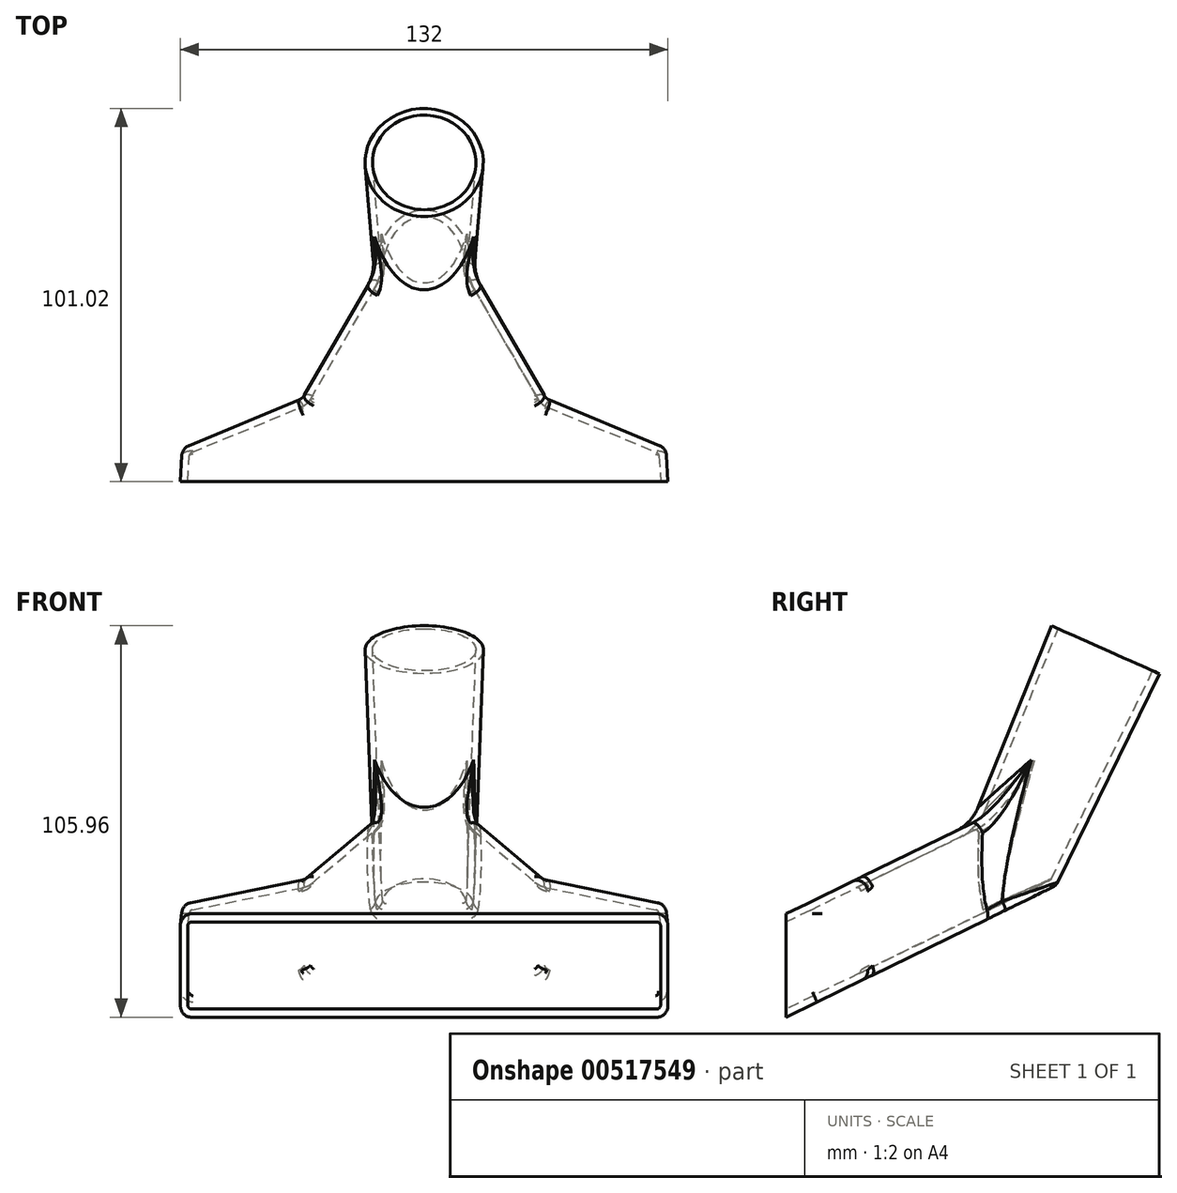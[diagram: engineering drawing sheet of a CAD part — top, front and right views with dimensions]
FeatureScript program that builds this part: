
annotation { "Feature Type Name" : "Feature", "Feature Type Description" : "" }
export const myFeature = defineFeature(function(context is Context, id is Id, definition is map)
    precondition{}
    {
        {
            var Q0;
            Q0=qCreatedBy(makeId("Right.planeOp"),FACE);
            var sketch = newSketch(context, id + "F0", { "sketchPlane" : qUnion([Q0])});
            skLineSegment(sketch, "E0", {"start": v(0, 0) * mm, "end": v(61.84, 30.16) * mm});
            skLineSegment(sketch, "E1", {"start": v(61.84, 30.16) * mm, "end": v(86.44, 85.43) * mm});
            skLineSegment(sketch, "E2", {"start": v(50.13, 0) * mm, "end": v(-17.29, 0) * mm, "construction": true});
            skSolve(sketch);
        }
        {
            var Q0;
            Q0=qCreatedBy(makeId("Top.planeOp"),FACE);
            var sketch = newSketch(context, id + "F1", { "sketchPlane" : qUnion([Q0])});
            skPoint(sketch, "E3", {"position": v(56.62, 0) * mm});
            skSolve(sketch);
        }
        {
            var Q0;
            Q0=sQuery(id+"F1.wireOp",VERTEX,"E3");
            var Q1;
            Q1=sQuery(id+"F0.wireOp",VERTEX,"E1.start");
            var Q2;
            Q2=sQuery(id+"F0.wireOp",VERTEX,"E0.start");
            cPlane(context, id + "F2", {"entities" : qUnion([Q0, Q1, Q2]), "cplaneType" : CPlaneType.THREE_POINT, "offset" : 25 * mm, "width" : 150 * mm, "height" : 150 * mm});
        }
        {
            var Q0;
            Q0=qCreatedBy(id+"F2.planeOp",FACE);
            var sketch = newSketch(context, id + "F3", { "sketchPlane" : qUnion([Q0])});
            skLineSegment(sketch, "E4", {"start": v(66, 0) * mm, "end": v(65.48, -10) * mm});
            skLineSegment(sketch, "E5", {"start": v(10.62, -68) * mm, "end": v(33, -25) * mm});
            skLineSegment(sketch, "E6", {"start": v(0, 33.94) * mm, "end": v(0, -95.34) * mm, "construction": true});
            skLineSegment(sketch, "E7.MirrorCS", {"start": v(-66, 0) * mm, "end": v(-65.48, -10) * mm});
            skLineSegment(sketch, "E8.MirrorCS", {"start": v(-65.48, -10) * mm, "end": v(-33, -25) * mm});
            skLineSegment(sketch, "E9.MirrorCS", {"start": v(-10.62, -68) * mm, "end": v(-33, -25) * mm});
            skLineSegment(sketch, "E10", {"start": v(66, 0) * mm, "end": v(-66, 0) * mm});
            skLineSegment(sketch, "E11", {"start": v(10.62, -68) * mm, "end": v(-10.62, -68) * mm});
            skLineSegment(sketch, "E12", {"start": v(65.48, -10) * mm, "end": v(33, -25) * mm});
            skSolve(sketch);
        }
        {
            var Q0;
            Q0=qCreatedBy(makeId("Front.planeOp"),FACE);
            var sketch = newSketch(context, id + "F4", { "sketchPlane" : qUnion([Q0])});
            skLineSegment(sketch, "E13", {"start": v(0, 0) * mm, "end": v(0, 14) * mm});
            skSolve(sketch);
        }
        {
            var Q0;
            Q0=qCreatedBy(makeId("Front.planeOp"),FACE);
            var sketch = newSketch(context, id + "F5", { "sketchPlane" : qUnion([Q0])});
            skLineSegment(sketch, "E14", {"start": v(0, 0) * mm, "end": v(0, -14) * mm});
            skSolve(sketch);
        }
        {
            var Q0;
            Q0 = qSketchRegion(id + "F3", true);
            var Q1;
            Q1=sQuery(id+"F4.wireOp",EDGE,"E13");
            sweep(context, id + "F6", {"profiles" : qUnion([Q0]), "path" : qUnion([Q1])});
        }
        {
            var Q0;
            Q0 = qSketchRegion(id + "F3", true);
            var Q1;
            Q1=sQuery(id+"F5.wireOp",EDGE,"E14");
            sweep(context, id + "F7", {"operationType" : NewBodyOperationType.ADD, "profiles" : qUnion([Q0]), "path" : qUnion([Q1])});
        }
        {
            var Q0;
            Q0=sQuery(id+"F0.wireOp",EDGE,"E1");
            var Q1;
            Q1=sQuery(id+"F0.wireOp",VERTEX,"E1.end");
            cPlane(context, id + "F8", {"entities" : qUnion([Q0, Q1]), "cplaneType" : CPlaneType.LINE_POINT, "offset" : 25 * mm, "width" : 150 * mm, "height" : 150 * mm});
        }
        {
            var Q0;
            Q0=qCreatedBy(id+"F8.planeOp",FACE);
            var sketch = newSketch(context, id + "F9", { "sketchPlane" : qUnion([Q0])});
            skPoint(sketch, "E15.0", {"position": v(0, 44.22) * mm});
            skCircle(sketch, "E16", {"center": v(0, 44.17) * mm, "radius": 16 * mm});
            skSolve(sketch);
        }
        {
            var Q0;
            Q0 = qSketchRegion(id + "F9", true);
            var Q1;
            Q1=makeQuery(id+"F7.opSweep","CAP_FACE",FACE,{"disambiguationData":[OSD([sQuery(id+"F3.wireOp",EDGE,"E4"),sQuery(id+"F3.wireOp",EDGE,"E5"),sQuery(id+"F3.wireOp",EDGE,"E7.MirrorCS"),sQuery(id+"F3.wireOp",EDGE,"E8.MirrorCS"),sQuery(id+"F3.wireOp",EDGE,"E9.MirrorCS"),sQuery(id+"F3.wireOp",EDGE,"E10"),sQuery(id+"F3.wireOp",EDGE,"E11"),sQuery(id+"F3.wireOp",EDGE,"E12"),sQuery(id+"F5.wireOp",VERTEX,"E14.end")])],"isStart":false});
            var Q2;
            Q2=makeQuery(id+"F7.opSweep","CAP_VERTEX",VERTEX,{"disambiguationData":[OSD([sQuery(id+"F3.wireOp",EDGE,"E5"),sQuery(id+"F3.wireOp",EDGE,"E11"),sQuery(id+"F5.wireOp",EDGE,"E14")])],"isStart":false});
            extrude(context, id + "F10", {"entities" : qUnion([Q0]), "operationType" : NewBodyOperationType.ADD, "endBound" : BoundingType.UP_TO_SURFACE, "oppositeDirection" : true, "depth" : 25 * mm, "endBoundEntityFace" : qUnion([Q1]), "endBoundEntityVertex" : qUnion([Q2]), "offsetDistance" : 25 * mm, "hasDraft" : true, "draftAngle" : 2 * degree, "draftPullDirection" : true});
        }
        {
            var Q0;
            Q0=makeQuery(id+"F10.boolean.opBoolean","INTERSECT",EDGE,{"derivedFrom":[makeQuery(id+"F6.opSweep","CAP_FACE",FACE,{"disambiguationData":[OSD([sQuery(id+"F3.wireOp",EDGE,"E4"),sQuery(id+"F3.wireOp",EDGE,"E5"),sQuery(id+"F3.wireOp",EDGE,"E7.MirrorCS"),sQuery(id+"F3.wireOp",EDGE,"E8.MirrorCS"),sQuery(id+"F3.wireOp",EDGE,"E9.MirrorCS"),sQuery(id+"F3.wireOp",EDGE,"E10"),sQuery(id+"F3.wireOp",EDGE,"E11"),sQuery(id+"F3.wireOp",EDGE,"E12"),sQuery(id+"F4.wireOp",VERTEX,"E13.end")])],"isStart":false}),makeQuery(id+"F10.opExtrude","SWEPT_FACE",FACE,{"disambiguationData":[OSD([sQuery(id+"F9.wireOp",EDGE,"E16")])]})]});
            var Q1;
            {var subQ0=sQuery(id+"F3.wireOp",EDGE,"E5");Q1=makeQuery(id+"F10.boolean.opBoolean","INTERSECT",EDGE,{"derivedFrom":[makeQuery(id+"F7.boolean.opBoolean","MERGE",FACE,{"derivedFrom":[makeQuery(id+"F6.opSweep","SWEPT_FACE",FACE,{"disambiguationData":[OSD([subQ0,sQuery(id+"F4.wireOp",EDGE,"E13")])]}),makeQuery(id+"F7.opSweep","SWEPT_FACE",FACE,{"disambiguationData":[OSD([subQ0,sQuery(id+"F5.wireOp",EDGE,"E14")])]})]}),makeQuery(id+"F10.opExtrude","SWEPT_FACE",FACE,{"disambiguationData":[OSD([sQuery(id+"F9.wireOp",EDGE,"E16")])]})]});}
            var Q2;
            {var subQ0=sQuery(id+"F3.wireOp",EDGE,"E9.MirrorCS");Q2=makeQuery(id+"F10.boolean.opBoolean","INTERSECT",EDGE,{"derivedFrom":[makeQuery(id+"F7.boolean.opBoolean","MERGE",FACE,{"derivedFrom":[makeQuery(id+"F6.opSweep","SWEPT_FACE",FACE,{"disambiguationData":[OSD([subQ0,sQuery(id+"F4.wireOp",EDGE,"E13")])]}),makeQuery(id+"F7.opSweep","SWEPT_FACE",FACE,{"disambiguationData":[OSD([subQ0,sQuery(id+"F5.wireOp",EDGE,"E14")])]})]}),makeQuery(id+"F10.opExtrude","SWEPT_FACE",FACE,{"disambiguationData":[OSD([sQuery(id+"F9.wireOp",EDGE,"E16")])]})]});}
            fillet(context, id + "F11", {"entities" : qUnion([Q0, Q1, Q2]), "radius" : 12 * mm, "tangentPropagation" : true, "allowEdgeOverflow" : false});
        }
        {
            var Q0;
            Q0=makeQuery(id+"F6.opSweep","CAP_EDGE",EDGE,{"disambiguationData":[OSD([sQuery(id+"F3.wireOp",EDGE,"E5"),sQuery(id+"F4.wireOp",VERTEX,"E13.end")])],"isStart":false});
            var Q1;
            Q1=makeQuery(id+"F6.opSweep","CAP_EDGE",EDGE,{"disambiguationData":[OSD([sQuery(id+"F3.wireOp",EDGE,"E12"),sQuery(id+"F4.wireOp",VERTEX,"E13.end")])],"isStart":false});
            var Q2;
            {var subQ0=sQuery(id+"F3.wireOp",EDGE,"E12");var subQ1=sQuery(id+"F3.wireOp",EDGE,"E4");Q2=makeQuery(id+"F7.boolean.opBoolean","MERGE",EDGE,{"derivedFrom":[makeQuery(id+"F6.opSweep","SWEPT_EDGE",EDGE,{"disambiguationData":[OSD([subQ1,subQ0,sQuery(id+"F4.wireOp",EDGE,"E13")])]}),makeQuery(id+"F7.opSweep","SWEPT_EDGE",EDGE,{"disambiguationData":[OSD([subQ1,subQ0,sQuery(id+"F5.wireOp",EDGE,"E14")])]})]});}
            var Q3;
            Q3=makeQuery(id+"F6.opSweep","CAP_EDGE",EDGE,{"disambiguationData":[OSD([sQuery(id+"F3.wireOp",EDGE,"E4"),sQuery(id+"F4.wireOp",VERTEX,"E13.end")])],"isStart":false});
            var Q4;
            Q4=makeQuery(id+"F7.opSweep","CAP_EDGE",EDGE,{"disambiguationData":[OSD([sQuery(id+"F3.wireOp",EDGE,"E4"),sQuery(id+"F5.wireOp",VERTEX,"E14.end")])],"isStart":false});
            var Q5;
            Q5=makeQuery(id+"F7.opSweep","CAP_EDGE",EDGE,{"disambiguationData":[OSD([sQuery(id+"F3.wireOp",EDGE,"E5"),sQuery(id+"F5.wireOp",VERTEX,"E14.end")])],"isStart":false});
            var Q6;
            Q6=makeQuery(id+"F7.opSweep","CAP_EDGE",EDGE,{"disambiguationData":[OSD([sQuery(id+"F3.wireOp",EDGE,"E12"),sQuery(id+"F5.wireOp",VERTEX,"E14.end")])],"isStart":false});
            var Q7;
            Q7=makeQuery(id+"F7.opSweep","CAP_EDGE",EDGE,{"disambiguationData":[OSD([sQuery(id+"F3.wireOp",EDGE,"E8.MirrorCS"),sQuery(id+"F5.wireOp",VERTEX,"E14.end")])],"isStart":false});
            var Q8;
            {var subQ0=sQuery(id+"F3.wireOp",EDGE,"E9.MirrorCS");var subQ1=sQuery(id+"F3.wireOp",EDGE,"E8.MirrorCS");Q8=makeQuery(id+"F7.boolean.opBoolean","MERGE",EDGE,{"derivedFrom":[makeQuery(id+"F6.opSweep","SWEPT_EDGE",EDGE,{"disambiguationData":[OSD([subQ1,subQ0,sQuery(id+"F4.wireOp",EDGE,"E13")])]}),makeQuery(id+"F7.opSweep","SWEPT_EDGE",EDGE,{"disambiguationData":[OSD([subQ1,subQ0,sQuery(id+"F5.wireOp",EDGE,"E14")])]})]});}
            var Q9;
            {var subQ0=sQuery(id+"F3.wireOp",EDGE,"E8.MirrorCS");var subQ1=sQuery(id+"F3.wireOp",EDGE,"E7.MirrorCS");Q9=makeQuery(id+"F7.boolean.opBoolean","MERGE",EDGE,{"derivedFrom":[makeQuery(id+"F6.opSweep","SWEPT_EDGE",EDGE,{"disambiguationData":[OSD([subQ1,subQ0,sQuery(id+"F4.wireOp",EDGE,"E13")])]}),makeQuery(id+"F7.opSweep","SWEPT_EDGE",EDGE,{"disambiguationData":[OSD([subQ1,subQ0,sQuery(id+"F5.wireOp",EDGE,"E14")])]})]});}
            var Q10;
            Q10=makeQuery(id+"F7.opSweep","CAP_EDGE",EDGE,{"disambiguationData":[OSD([sQuery(id+"F3.wireOp",EDGE,"E7.MirrorCS"),sQuery(id+"F5.wireOp",VERTEX,"E14.end")])],"isStart":false});
            var Q11;
            Q11=makeQuery(id+"F6.opSweep","CAP_EDGE",EDGE,{"disambiguationData":[OSD([sQuery(id+"F3.wireOp",EDGE,"E9.MirrorCS"),sQuery(id+"F4.wireOp",VERTEX,"E13.end")])],"isStart":false});
            var Q12;
            Q12=makeQuery(id+"F6.opSweep","CAP_EDGE",EDGE,{"disambiguationData":[OSD([sQuery(id+"F3.wireOp",EDGE,"E7.MirrorCS"),sQuery(id+"F4.wireOp",VERTEX,"E13.end")])],"isStart":false});
            var Q13;
            {var subQ0=sQuery(id+"F3.wireOp",EDGE,"E12");var subQ1=sQuery(id+"F3.wireOp",EDGE,"E5");Q13=makeQuery(id+"F7.boolean.opBoolean","MERGE",EDGE,{"derivedFrom":[makeQuery(id+"F6.opSweep","SWEPT_EDGE",EDGE,{"disambiguationData":[OSD([subQ1,subQ0,sQuery(id+"F4.wireOp",EDGE,"E13")])]}),makeQuery(id+"F7.opSweep","SWEPT_EDGE",EDGE,{"disambiguationData":[OSD([subQ1,subQ0,sQuery(id+"F5.wireOp",EDGE,"E14")])]})]});}
            var Q14;
            Q14=makeQuery(id+"F10.opExtrude","TWEAK_EDGE",EDGE,{"derivedFrom":[makeQuery(id+"F7.opSweep","CAP_FACE",FACE,{"disambiguationData":[OSD([sQuery(id+"F3.wireOp",EDGE,"E4"),sQuery(id+"F3.wireOp",EDGE,"E5"),sQuery(id+"F3.wireOp",EDGE,"E7.MirrorCS"),sQuery(id+"F3.wireOp",EDGE,"E8.MirrorCS"),sQuery(id+"F3.wireOp",EDGE,"E9.MirrorCS"),sQuery(id+"F3.wireOp",EDGE,"E10"),sQuery(id+"F3.wireOp",EDGE,"E11"),sQuery(id+"F3.wireOp",EDGE,"E12"),sQuery(id+"F5.wireOp",VERTEX,"E14.end")])],"isStart":false}),makeQuery(id+"F9.imprint","IMPRINT",EDGE,{"derivedFrom":sQuery(id+"F9.wireOp",EDGE,"E16")})]});
            var Q15;
            Q15=makeQuery(id+"F7.opSweep","CAP_EDGE",EDGE,{"disambiguationData":[OSD([sQuery(id+"F3.wireOp",EDGE,"E9.MirrorCS"),sQuery(id+"F5.wireOp",VERTEX,"E14.end")])],"isStart":false});
            var Q16;
            {var subQ0=sQuery(id+"F5.wireOp",VERTEX,"E14.end");var subQ1=sQuery(id+"F3.wireOp",EDGE,"E12");var subQ2=sQuery(id+"F3.wireOp",EDGE,"E11");var subQ3=sQuery(id+"F3.wireOp",EDGE,"E10");var subQ4=sQuery(id+"F3.wireOp",EDGE,"E9.MirrorCS");var subQ5=sQuery(id+"F3.wireOp",EDGE,"E8.MirrorCS");var subQ6=sQuery(id+"F3.wireOp",EDGE,"E7.MirrorCS");var subQ7=sQuery(id+"F3.wireOp",EDGE,"E5");var subQ8=sQuery(id+"F3.wireOp",EDGE,"E4");Q16=makeQuery(id+"F11.opFillet","BLEND_EDGE",EDGE,{"blendedFrom":[makeQuery(id+"F10.boolean.opBoolean","INTERSECT",EDGE,{"derivedFrom":[makeQuery(id+"F7.boolean.opBoolean","MERGE",FACE,{"derivedFrom":[makeQuery(id+"F6.opSweep","SWEPT_FACE",FACE,{"disambiguationData":[OSD([subQ4,sQuery(id+"F4.wireOp",EDGE,"E13")])]}),makeQuery(id+"F7.opSweep","SWEPT_FACE",FACE,{"disambiguationData":[OSD([subQ4,sQuery(id+"F5.wireOp",EDGE,"E14")])]})]}),makeQuery(id+"F10.opExtrude","SWEPT_FACE",FACE,{"disambiguationData":[OSD([sQuery(id+"F9.wireOp",EDGE,"E16")])]})]}),makeQuery(id+"F10.boolean.opBoolean","MERGE",FACE,{"derivedFrom":[makeQuery(id+"F7.opSweep","CAP_FACE",FACE,{"disambiguationData":[OSD([subQ8,subQ7,subQ6,subQ5,subQ4,subQ3,subQ2,subQ1,subQ0])],"isStart":false}),makeQuery(id+"F10.opExtrude","CAP_FACE",FACE,{"disambiguationData":[OSD([subQ8,subQ7,subQ6,subQ5,subQ4,subQ3,subQ2,subQ1,subQ0])],"isStart":false})]})],"blendedInto":[makeQuery(id+"F10.boolean.opBoolean","MERGE",FACE,{"derivedFrom":[makeQuery(id+"F7.opSweep","CAP_FACE",FACE,{"disambiguationData":[OSD([subQ8,subQ7,subQ6,subQ5,subQ4,subQ3,subQ2,subQ1,subQ0])],"isStart":false}),makeQuery(id+"F10.opExtrude","CAP_FACE",FACE,{"disambiguationData":[OSD([subQ8,subQ7,subQ6,subQ5,subQ4,subQ3,subQ2,subQ1,subQ0])],"isStart":false})]})]});}
            var Q17;
            {var subQ0=sQuery(id+"F5.wireOp",VERTEX,"E14.end");var subQ1=sQuery(id+"F3.wireOp",EDGE,"E12");var subQ2=sQuery(id+"F3.wireOp",EDGE,"E11");var subQ3=sQuery(id+"F3.wireOp",EDGE,"E10");var subQ4=sQuery(id+"F3.wireOp",EDGE,"E9.MirrorCS");var subQ5=sQuery(id+"F3.wireOp",EDGE,"E8.MirrorCS");var subQ6=sQuery(id+"F3.wireOp",EDGE,"E7.MirrorCS");var subQ7=sQuery(id+"F3.wireOp",EDGE,"E5");var subQ8=sQuery(id+"F3.wireOp",EDGE,"E4");Q17=makeQuery(id+"F11.opFillet","BLEND_EDGE",EDGE,{"blendedFrom":[makeQuery(id+"F10.boolean.opBoolean","INTERSECT",EDGE,{"derivedFrom":[makeQuery(id+"F7.boolean.opBoolean","MERGE",FACE,{"derivedFrom":[makeQuery(id+"F6.opSweep","SWEPT_FACE",FACE,{"disambiguationData":[OSD([subQ7,sQuery(id+"F4.wireOp",EDGE,"E13")])]}),makeQuery(id+"F7.opSweep","SWEPT_FACE",FACE,{"disambiguationData":[OSD([subQ7,sQuery(id+"F5.wireOp",EDGE,"E14")])]})]}),makeQuery(id+"F10.opExtrude","SWEPT_FACE",FACE,{"disambiguationData":[OSD([sQuery(id+"F9.wireOp",EDGE,"E16")])]})]}),makeQuery(id+"F10.boolean.opBoolean","MERGE",FACE,{"derivedFrom":[makeQuery(id+"F7.opSweep","CAP_FACE",FACE,{"disambiguationData":[OSD([subQ8,subQ7,subQ6,subQ5,subQ4,subQ3,subQ2,subQ1,subQ0])],"isStart":false}),makeQuery(id+"F10.opExtrude","CAP_FACE",FACE,{"disambiguationData":[OSD([subQ8,subQ7,subQ6,subQ5,subQ4,subQ3,subQ2,subQ1,subQ0])],"isStart":false})]})],"blendedInto":[makeQuery(id+"F10.boolean.opBoolean","MERGE",FACE,{"derivedFrom":[makeQuery(id+"F7.opSweep","CAP_FACE",FACE,{"disambiguationData":[OSD([subQ8,subQ7,subQ6,subQ5,subQ4,subQ3,subQ2,subQ1,subQ0])],"isStart":false}),makeQuery(id+"F10.opExtrude","CAP_FACE",FACE,{"disambiguationData":[OSD([subQ8,subQ7,subQ6,subQ5,subQ4,subQ3,subQ2,subQ1,subQ0])],"isStart":false})]})]});}
            var Q18;
            Q18=makeQuery(id+"F6.opSweep","CAP_EDGE",EDGE,{"disambiguationData":[OSD([sQuery(id+"F3.wireOp",EDGE,"E8.MirrorCS"),sQuery(id+"F4.wireOp",VERTEX,"E13.end")])],"isStart":false});
            var Q19;
            {var subQ0=makeQuery(id+"F10.opExtrude","SWEPT_FACE",FACE,{"disambiguationData":[OSD([sQuery(id+"F9.wireOp",EDGE,"E16")])]});var subQ1=sQuery(id+"F3.wireOp",EDGE,"E9.MirrorCS");Q19=makeQuery(id+"F11.opFillet","BLEND_EDGE",EDGE,{"blendedFrom":[makeQuery(id+"F10.boolean.opBoolean","INTERSECT",EDGE,{"derivedFrom":[makeQuery(id+"F6.opSweep","CAP_FACE",FACE,{"disambiguationData":[OSD([sQuery(id+"F3.wireOp",EDGE,"E4"),sQuery(id+"F3.wireOp",EDGE,"E5"),sQuery(id+"F3.wireOp",EDGE,"E7.MirrorCS"),sQuery(id+"F3.wireOp",EDGE,"E8.MirrorCS"),subQ1,sQuery(id+"F3.wireOp",EDGE,"E10"),sQuery(id+"F3.wireOp",EDGE,"E11"),sQuery(id+"F3.wireOp",EDGE,"E12"),sQuery(id+"F4.wireOp",VERTEX,"E13.end")])],"isStart":false}),subQ0]}),makeQuery(id+"F10.boolean.opBoolean","INTERSECT",EDGE,{"derivedFrom":[makeQuery(id+"F7.boolean.opBoolean","MERGE",FACE,{"derivedFrom":[makeQuery(id+"F6.opSweep","SWEPT_FACE",FACE,{"disambiguationData":[OSD([subQ1,sQuery(id+"F4.wireOp",EDGE,"E13")])]}),makeQuery(id+"F7.opSweep","SWEPT_FACE",FACE,{"disambiguationData":[OSD([subQ1,sQuery(id+"F5.wireOp",EDGE,"E14")])]})]}),subQ0]})],"blendedInto":[]});}
            var Q20;
            {var subQ0=makeQuery(id+"F10.opExtrude","SWEPT_FACE",FACE,{"disambiguationData":[OSD([sQuery(id+"F9.wireOp",EDGE,"E16")])]});var subQ1=sQuery(id+"F3.wireOp",EDGE,"E5");Q20=makeQuery(id+"F11.opFillet","BLEND_EDGE",EDGE,{"blendedFrom":[makeQuery(id+"F10.boolean.opBoolean","INTERSECT",EDGE,{"derivedFrom":[makeQuery(id+"F6.opSweep","CAP_FACE",FACE,{"disambiguationData":[OSD([sQuery(id+"F3.wireOp",EDGE,"E4"),subQ1,sQuery(id+"F3.wireOp",EDGE,"E7.MirrorCS"),sQuery(id+"F3.wireOp",EDGE,"E8.MirrorCS"),sQuery(id+"F3.wireOp",EDGE,"E9.MirrorCS"),sQuery(id+"F3.wireOp",EDGE,"E10"),sQuery(id+"F3.wireOp",EDGE,"E11"),sQuery(id+"F3.wireOp",EDGE,"E12"),sQuery(id+"F4.wireOp",VERTEX,"E13.end")])],"isStart":false}),subQ0]}),makeQuery(id+"F10.boolean.opBoolean","INTERSECT",EDGE,{"derivedFrom":[makeQuery(id+"F7.boolean.opBoolean","MERGE",FACE,{"derivedFrom":[makeQuery(id+"F6.opSweep","SWEPT_FACE",FACE,{"disambiguationData":[OSD([subQ1,sQuery(id+"F4.wireOp",EDGE,"E13")])]}),makeQuery(id+"F7.opSweep","SWEPT_FACE",FACE,{"disambiguationData":[OSD([subQ1,sQuery(id+"F5.wireOp",EDGE,"E14")])]})]}),subQ0]})],"blendedInto":[]});}
            fillet(context, id + "F12", {"entities" : qUnion([Q0, Q1, Q2, Q3, Q4, Q5, Q6, Q7, Q8, Q9, Q10, Q11, Q12, Q13, Q14, Q15, Q16, Q17, Q18, Q19, Q20]), "radius" : 3 * mm, "tangentPropagation" : true, "allowEdgeOverflow" : false});
        }
        {
            var Q0;
            {var subQ0=sQuery(id+"F3.wireOp",EDGE,"E10");Q0=makeQuery(id+"F7.boolean.opBoolean","MERGE",FACE,{"derivedFrom":[makeQuery(id+"F6.opSweep","SWEPT_FACE",FACE,{"disambiguationData":[OSD([subQ0,sQuery(id+"F4.wireOp",EDGE,"E13")])]}),makeQuery(id+"F7.opSweep","SWEPT_FACE",FACE,{"disambiguationData":[OSD([subQ0,sQuery(id+"F5.wireOp",EDGE,"E14")])]})]});}
            var Q1;
            Q1=makeQuery(id+"F10.opExtrude","CAP_FACE",FACE,{"disambiguationData":[OSD([sQuery(id+"F9.wireOp",EDGE,"E16")])],"isStart":true});
            shell(context, id + "F13", {"entities" : qUnion([Q0, Q1]), "thickness" : 2 * mm});
        }
    });
